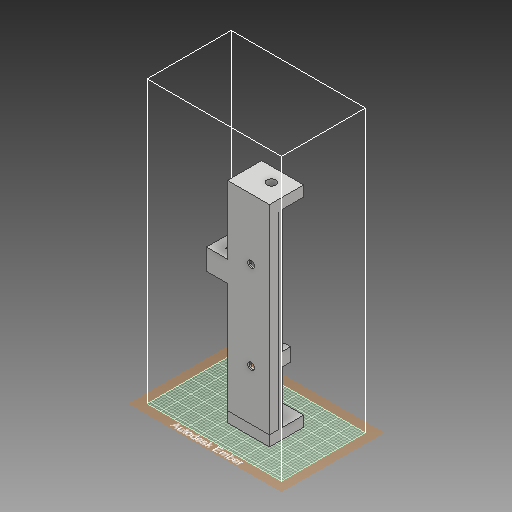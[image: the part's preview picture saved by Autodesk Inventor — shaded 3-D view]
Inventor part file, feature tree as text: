
AUTODESK INVENTOR PART (.ipt)
format: ipt  version: 2018 (Build 220112000, 112)  size: 569,856 bytes
history: native  units: mm
features: sketch x34, extrude x23, hole x7, fillet x5
ambient origin geometry x8: Origin, YZ Plane, XZ Plane, XY Plane, X Axis, Y Axis, Z Axis, Center Point
bodies: Solid1 (feature_tree)
feature tree (69):
  extrude  "Extrusion1"  Depth=100.0mm
  extrude  "Extrusion2"  Depth=5.0mm
  sketch  "Sketch3"  dims[d5=5.0mm d6=40.0mm d7=0.0mm]
  hole  "Hole1"  [1 undecoded]
  extrude  "Extrusion3"  Depth=2.0mm
  hole  "Hole2"  [1 undecoded]
  fillet  "Fillet1"  Radius=8.5mm
  extrude  "Extrusion4"  TaperAngle=90.0deg  [1 undecoded]
  extrude  "Extrusion5"  TaperAngle=180.0deg  [1 undecoded]
  hole  "Hole3"  [1 undecoded]
  fillet  "Fillet2"  Radius=3.5mm
  extrude  "Extrusion6"  Depth=10.0mm
  extrude  "Extrusion7"  Depth=5.0mm TaperAngle=0.0deg
  extrude  "Extrusion8"  Depth=12.5mm TaperAngle=0.0deg
  extrude  "Extrusion9"  Depth=0.1mm
  hole  "Hole4"  [1 undecoded]
  extrude  "Extrusion10"  Depth=5.5mm
  hole  "Hole5"  [1 undecoded]
  extrude  "Extrusion11"  Depth=2.1mm TaperAngle=0.0deg
  extrude  "Extrusion12"  Depth=5.0mm
  extrude  "Extrusion13"  Depth=1.0mm TaperAngle=0.0deg
  extrude  "Extrusion14"  Depth=3.8mm TaperAngle=0.0deg
  sketch  "Sketch21"  dims[d66=6.35mm d67=3.8mm d68=0.0mm]
  extrude  "Extrusion15"  Depth=2.0mm TaperAngle=0.0deg
  sketch  "Sketch23"  dims[d78=3.3mm d79=6.0mm d80=4.0mm d81=2.0mm d82=90.0deg d83=80.0mm d84=20.594885mm d85=5.45mm]
  extrude  "Extrusion16"  Depth=2.0mm
  extrude  "Extrusion17"  Depth=10.5mm
  hole  "Hole6"  [1 undecoded]
  fillet  "Fillet3"  Radius=4.5mm
  extrude  "Extrusion18"  Depth=15.5mm TaperAngle=0.0deg
  sketch  "Sketch28"  dims[d100=4.1mm d101=0.0mm d102=5.0mm]
  extrude  "Extrusion19"  Depth=10.0mm
  extrude  "Extrusion20"  Depth=5.0mm
  extrude  "Extrusion21"  Depth=10.0mm TaperAngle=0.0deg
  hole  "Hole7"  [1 undecoded]
  extrude  "Extrusion22"  Depth=21.0mm
  extrude  "Extrusion23"  Depth=118.0mm TaperAngle=0.0deg
  fillet  "Fillet4"  Radius=50.0mm
  fillet  "Fillet5"  Radius=7.499983mm
  sketch  "Sketch1"  dims[d0=22.65mm d1=100.0mm]
  sketch  "Sketch2"  dims[d2=5.0mm d3=0.0mm d4=5.0mm]
  sketch  "Sketch4"  dims[d8=10.0mm]
  sketch  "Sketch5"  dims[d9=4.0mm d10=6.0mm d11=4.0mm d12=2.0mm d13=90.0deg d14=115.0mm d15=20.594885mm d16=23.0mm]
  sketch  "Sketch6"  dims[d17=102.75mm d18=0.0mm d19=1.175mm d20=8.5mm]
  sketch  "Sketch7"  dims[d21=21.0mm d22=90.0deg]
  sketch  "Sketch8"  dims[d23=8.5mm d24=180.0deg]
  sketch  "Sketch9"  dims[d25=21.0mm]
  sketch  "Sketch10"  dims[d26=4.0mm d27=6.0mm d28=4.0mm d29=2.0mm d30=90.0deg d31=115.0mm d32=20.594885mm d33=1.0mm d34=3.5mm]
  sketch  "Sketch11"  dims[d35=15.825mm d36=10.0mm]
  sketch  "Sketch12"  dims[d37=10.0mm d38=5.0mm d39=0.0mm]
  sketch  "Sketch13"  dims[d40=5.0mm d41=12.5mm d42=0.0mm]
  sketch  "Sketch14"  dims[d43=6.0mm d44=6.0mm d45=4.0mm d46=2.0mm d47=90.0deg d48=115.0mm d49=20.594885mm d50=0.1mm]
  sketch  "Sketch15"  dims[d51=4.25mm d52=1000.0mm d53=0.0mm]
  sketch  "Sketch16"  dims[d54=3.3mm d55=5.5mm]
  sketch  "Sketch17"  dims[d56=3.2mm d57=3.0mm]
  sketch  "Sketch18"  dims[d58=2.1mm d59=91.25mm d60=0.0mm]
  sketch  "Sketch19"  dims[d61=4.44mm d62=5.0mm]
  sketch  "Sketch20"  dims[d63=1.0mm d64=91.25mm d65=0.0mm]
  sketch  "Sketch22"  dims[d69=3.3mm d70=6.0mm d71=4.0mm d72=2.0mm d73=90.0deg d74=8.0mm d75=20.594885mm d76=4.55mm d77=0.0mm]
  sketch  "Sketch24"  dims[d86=129.8mm d87=0.0mm d88=10.5mm]
  sketch  "Sketch25"  dims[d89=2.5mm d90=0.0mm d91=10.0mm d92=4.5mm d93=0.0mm]
  sketch  "Sketch26"  dims[d94=8.0mm d95=0.0mm d96=15.5mm d97=0.0mm]
  sketch  "Sketch27"  dims[d98=10.0mm d99=10.0mm]
  sketch  "Sketch29"  dims[d103=17.5mm d104=10.0mm d105=0.0mm]
  sketch  "Sketch30"  dims[d106=5.0mm]
  sketch  "Sketch31"  dims[d107=6.0mm d108=6.0mm d109=4.0mm d110=2.0mm d111=90.0deg d112=80.0mm d113=20.594885mm d114=2.0mm]
  sketch  "Sketch32"  dims[d115=45.0mm d116=0.0mm d117=21.0mm]
  sketch  "Sketch33"  dims[d118=4.5mm d119=118.0mm d120=0.0mm d121=50.0mm d122=7.499983mm]
  sketch  "Sketch34"  dims[d123=7.5mm d124=10.0mm d125=10.0mm d126=4.1mm d127=0.0mm d128=13.4mm d129=0.0mm d130=5.0mm d131=6.0mm d132=6.0mm d133=4.0mm d134=2.0mm d135=90.0deg d136=8.0mm d137=20.594885mm d138=130.4mm d139=0.0mm d140=1.0mm d141=1.0mm d142=3.85mm d143=0.0mm d144=3.0mm d145=2.0mm]
note: 9 required parameter values undecoded (feature->parameter linkage not recoverable at this tier; creation-order binding heuristic only, values carry confidence <= 0.55)
